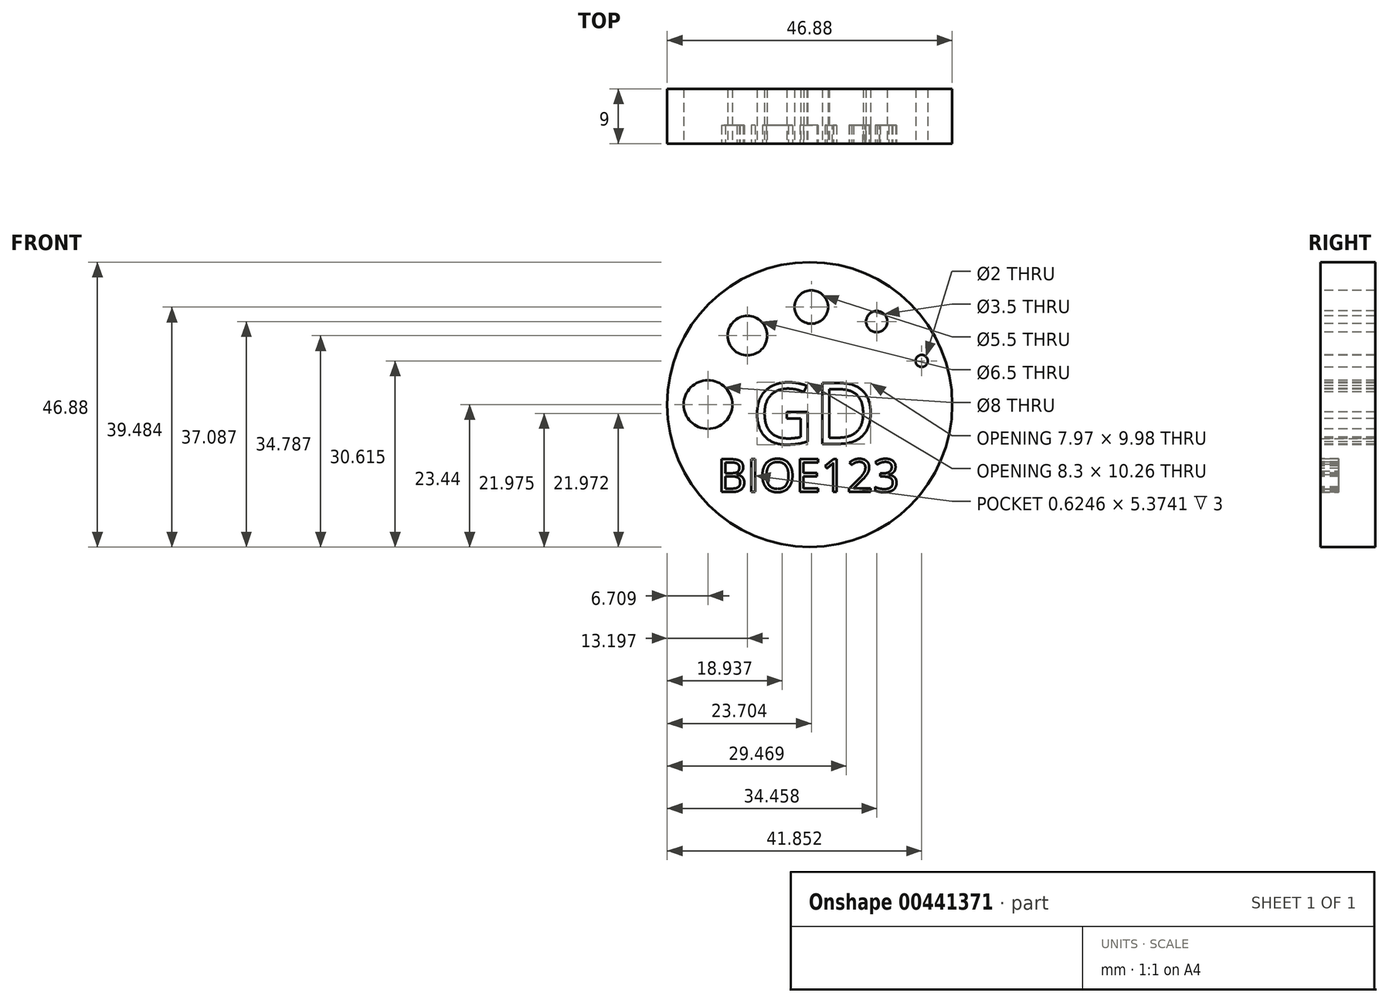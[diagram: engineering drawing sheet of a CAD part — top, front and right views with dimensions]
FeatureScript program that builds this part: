
annotation { "Feature Type Name" : "Feature", "Feature Type Description" : "" }
export const myFeature = defineFeature(function(context is Context, id is Id, definition is map)
    precondition{}
    {
        {
            var Q0;
            Q0=qCreatedBy(makeId("Front.planeOp"),FACE);
            var sketch = newSketch(context, id + "F0", { "sketchPlane" : qUnion([Q0])});
            skCircle(sketch, "E0", {"center": v(0, 0) * mm, "radius": 23.44 * mm});
            skSolve(sketch);
        }
        {
            var Q0;
            Q0=qSketchRegion(id+"F0",true);
            extrude(context, id + "F1", {"entities" : qUnion([Q0]), "oppositeDirection" : true, "depth" : 9 * mm});
        }
        {
            var Q0;
            Q0=qCreatedBy(makeId("Front.planeOp"),FACE);
            var sketch = newSketch(context, id + "F2", { "sketchPlane" : qUnion([Q0])});
            skCircle(sketch, "E1", {"center": v(-16.73, 0) * mm, "radius": 4 * mm});
            skCircle(sketch, "E2", {"center": v(-10.24, 11.35) * mm, "radius": 3.25 * mm});
            skCircle(sketch, "E3", {"center": v(0.26, 16.04) * mm, "radius": 2.75 * mm});
            skCircle(sketch, "E4", {"center": v(11.02, 13.65) * mm, "radius": 1.75 * mm});
            skCircle(sketch, "E5", {"center": v(18.41, 7.18) * mm, "radius": 1 * mm});
            skSolve(sketch);
        }
        {
            var Q0;
            Q0=qSketchRegion(id+"F2",true);
            extrude(context, id + "F3", {"entities" : qUnion([Q0]), "operationType" : NewBodyOperationType.REMOVE, "oppositeDirection" : true, "depth" : 9 * mm});
        }
        {
            var Q0;
            Q0=qCreatedBy(makeId("Front.planeOp"),FACE);
            var sketch = newSketch(context, id + "F4", { "sketchPlane" : qUnion([Q0])});
            skText(sketch, "E6", { "text": "GD", "fontName": "OpenSans-Regular.ttf"});
            const initialGuessF4  = {"E6": [-0.00951, -0.00646, 1, 0, 0.01007]};
            skSetInitialGuess(sketch, initialGuessF4);
            skSolve(sketch);
        }
        {
            var Q0;
            Q0=qSketchRegion(id+"F4",true);
            extrude(context, id + "F5", {"entities" : qUnion([Q0]), "operationType" : NewBodyOperationType.REMOVE, "oppositeDirection" : true, "depth" : 9 * mm});
        }
        {
            var Q0;
            Q0=qCreatedBy(makeId("Front.planeOp"),FACE);
            var sketch = newSketch(context, id + "F6", { "sketchPlane" : qUnion([Q0])});
            skText(sketch, "E7", { "text": "BIOE123", "fontName": "OpenSans-Regular.ttf"});
            const initialGuessF6  = {"E7": [-0.01522, -0.01436, 1, 0, 0.00542]};
            skSetInitialGuess(sketch, initialGuessF6);
            skSolve(sketch);
        }
        {
            var Q0;
            Q0 = qSketchRegion(id + "F6", true);
            extrude(context, id + "F7", {"entities" : qUnion([Q0]), "operationType" : NewBodyOperationType.REMOVE, "oppositeDirection" : true, "depth" : 3 * mm});
        }
    });
